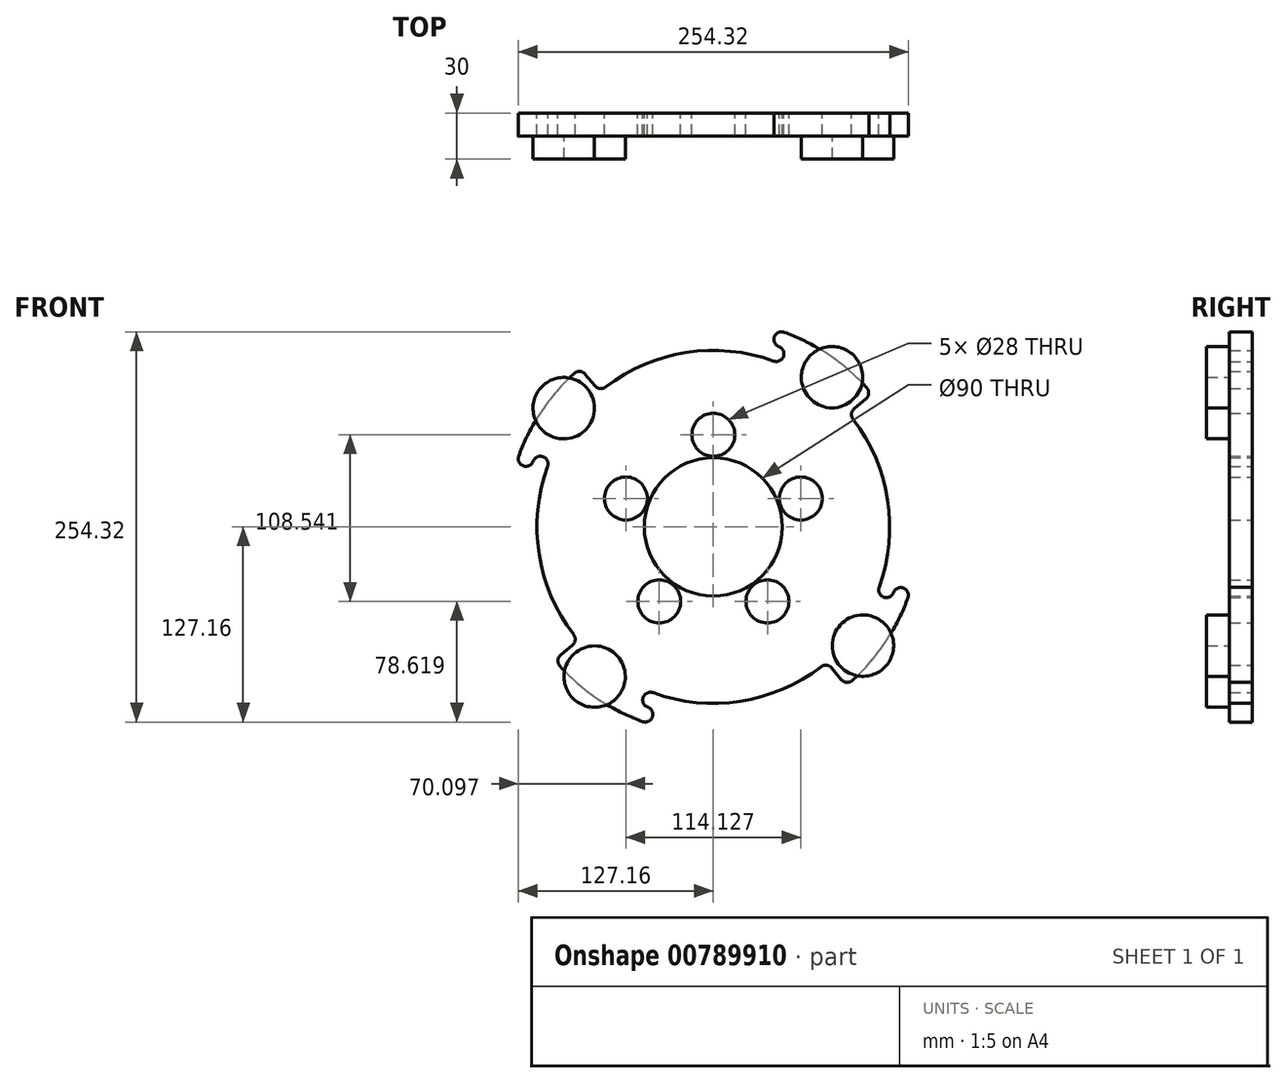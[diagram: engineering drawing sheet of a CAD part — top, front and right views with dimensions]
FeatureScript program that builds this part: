
annotation { "Feature Type Name" : "Feature", "Feature Type Description" : "" }
export const myFeature = defineFeature(function(context is Context, id is Id, definition is map)
    precondition{}
    {
        {
            var Q0;
            Q0=qCreatedBy(makeId("Front.planeOp"),FACE);
            var sketch = newSketch(context, id + "F0", { "sketchPlane" : qUnion([Q0])});
            skCircle(sketch, "E0", {"center": v(0, 0) * mm, "radius": 45 * mm});
            skCircle(sketch, "E1", {"center": v(0, 0) * mm, "radius": 60 * mm, "construction": true});
            skArc(sketch, "E2", {"start": v(-108.06, 39.33) * mm, "mid": v(-113.64, -17.6) * mm, "end": v(-91.1, -70.19) * mm});
            skArc(sketch, "E3", {"start": v(-90.69, 100) * mm, "mid": v(-112.05, 75.3) * mm, "end": v(-126.86, 46.17) * mm});
            skLineSegment(sketch, "E4", {"start": v(0, -160.96) * mm, "end": v(0, 165.3) * mm, "construction": true});
            skLineSegment(sketch, "E5", {"start": v(-181.36, 0) * mm, "end": v(230.59, 0) * mm, "construction": true});
            skLineSegment(sketch, "E6", {"start": v(0, 0) * mm, "end": v(-73.92, 88.1) * mm, "construction": true});
            skCircle(sketch, "E7", {"center": v(0, 60) * mm, "radius": 14 * mm});
            skCircle(sketch, "E8.1.0", {"center": v(-57.06, 18.54) * mm, "radius": 14 * mm});
            skCircle(sketch, "E8.2.0", {"center": v(-35.27, -48.54) * mm, "radius": 14 * mm});
            skCircle(sketch, "E8.3.0", {"center": v(35.27, -48.54) * mm, "radius": 14 * mm});
            skCircle(sketch, "E8.4.0", {"center": v(57.06, 18.54) * mm, "radius": 14 * mm});
            skLineSegment(sketch, "E9", {"start": v(0, 0) * mm, "end": v(-172.3, 62.71) * mm, "construction": true});
            skLineSegment(sketch, "E10", {"start": v(-77.07, 91.85) * mm, "end": v(-83.5, 99.51) * mm});
            skArc(sketch, "E11", {"start": v(-126.86, 46.17) * mm, "mid": v(-123.87, 39.76) * mm, "end": v(-117.46, 42.75) * mm});
            skArc(sketch, "E12", {"start": v(-108.06, 39.33) * mm, "mid": v(-111.05, 45.74) * mm, "end": v(-117.46, 42.75) * mm});
            skArc(sketch, "E13.1.0", {"start": v(-39.33, -108.06) * mm, "mid": v(-45.74, -111.05) * mm, "end": v(-42.75, -117.46) * mm});
            skArc(sketch, "E13.1.1", {"start": v(-46.17, -126.86) * mm, "mid": v(-39.76, -123.87) * mm, "end": v(-42.75, -117.46) * mm});
            skLineSegment(sketch, "E13.1.2", {"start": v(-91.85, -77.07) * mm, "end": v(-99.51, -83.5) * mm});
            skArc(sketch, "E13.2.0", {"start": v(108.06, -39.33) * mm, "mid": v(111.05, -45.74) * mm, "end": v(117.46, -42.75) * mm});
            skArc(sketch, "E13.2.1", {"start": v(126.86, -46.17) * mm, "mid": v(123.87, -39.76) * mm, "end": v(117.46, -42.75) * mm});
            skLineSegment(sketch, "E13.2.2", {"start": v(77.07, -91.85) * mm, "end": v(83.5, -99.51) * mm});
            skArc(sketch, "E13.3.0", {"start": v(39.33, 108.06) * mm, "mid": v(45.74, 111.05) * mm, "end": v(42.75, 117.46) * mm});
            skArc(sketch, "E13.3.1", {"start": v(46.17, 126.86) * mm, "mid": v(39.76, 123.87) * mm, "end": v(42.75, 117.46) * mm});
            skLineSegment(sketch, "E13.3.2", {"start": v(91.85, 77.07) * mm, "end": v(99.51, 83.5) * mm});
            skLineSegment(sketch, "E14.trimOffspring", {"start": v(-86.78, 103.42) * mm, "end": v(-114.3, 136.21) * mm, "construction": true});
            skArc(sketch, "E15.trimOffspring", {"start": v(100, 90.69) * mm, "mid": v(75.3, 112.05) * mm, "end": v(46.17, 126.86) * mm});
            skArc(sketch, "E16.trimOffspring", {"start": v(90.69, -100) * mm, "mid": v(112.05, -75.3) * mm, "end": v(126.86, -46.17) * mm});
            skArc(sketch, "E17.trimOffspring", {"start": v(-100, -90.69) * mm, "mid": v(-75.3, -112.05) * mm, "end": v(-46.17, -126.86) * mm});
            skPoint(sketch, "E18.visualSharp", {"position": v(-86.78, 103.42) * mm});
            skArc(sketch, "E18.filletArc", {"start": v(-83.5, 99.51) * mm, "mid": v(-87, 101.29) * mm, "end": v(-90.69, 100) * mm});
            skArc(sketch, "E19.trimOffspring", {"start": v(39.33, 108.06) * mm, "mid": v(-17.6, 113.64) * mm, "end": v(-70.19, 91.1) * mm});
            skArc(sketch, "E20.trimOffspring", {"start": v(108.06, -39.33) * mm, "mid": v(113.64, 17.6) * mm, "end": v(91.1, 70.19) * mm});
            skArc(sketch, "E21.trimOffspring", {"start": v(-39.33, -108.06) * mm, "mid": v(17.6, -113.64) * mm, "end": v(70.19, -91.1) * mm});
            skPoint(sketch, "E22.visualSharp", {"position": v(-73.92, 88.1) * mm});
            skArc(sketch, "E22.filletArc", {"start": v(-77.07, 91.85) * mm, "mid": v(-73.78, 90.09) * mm, "end": v(-70.19, 91.1) * mm});
            skPoint(sketch, "E23.visualSharp", {"position": v(-88.1, -73.92) * mm});
            skArc(sketch, "E23.filletArc", {"start": v(-91.85, -77.07) * mm, "mid": v(-90.09, -73.78) * mm, "end": v(-91.1, -70.19) * mm});
            skPoint(sketch, "E24.visualSharp", {"position": v(-103.42, -86.78) * mm});
            skArc(sketch, "E24.filletArc", {"start": v(-99.51, -83.5) * mm, "mid": v(-101.29, -87) * mm, "end": v(-100, -90.69) * mm});
            skPoint(sketch, "E25.visualSharp", {"position": v(73.92, -88.1) * mm});
            skArc(sketch, "E25.filletArc", {"start": v(77.07, -91.85) * mm, "mid": v(73.78, -90.09) * mm, "end": v(70.19, -91.1) * mm});
            skPoint(sketch, "E26.visualSharp", {"position": v(86.78, -103.42) * mm});
            skArc(sketch, "E26.filletArc", {"start": v(83.5, -99.51) * mm, "mid": v(87, -101.29) * mm, "end": v(90.69, -100) * mm});
            skPoint(sketch, "E27.visualSharp", {"position": v(103.42, 86.78) * mm});
            skArc(sketch, "E27.filletArc", {"start": v(99.51, 83.5) * mm, "mid": v(101.29, 87) * mm, "end": v(100, 90.69) * mm});
            skPoint(sketch, "E28.visualSharp", {"position": v(88.1, 73.92) * mm});
            skArc(sketch, "E28.filletArc", {"start": v(91.85, 77.07) * mm, "mid": v(90.09, 73.78) * mm, "end": v(91.1, 70.19) * mm});
            skSolve(sketch);
        }
        {
            var Q0;
            Q0=qSketchRegion(id+"F0",true);
            extrude(context, id + "F1", {"entities" : qUnion([Q0]), "depth" : 15 * mm, "offsetDistance" : 25 * mm});
        }
        {
            var Q0;
            Q0=makeQuery(id+"F1.opExtrude","CAP_FACE",FACE,{"disambiguationData":[OSD([sQuery(id+"F0.wireOp",EDGE,"E0"),sQuery(id+"F0.wireOp",EDGE,"E2"),sQuery(id+"F0.wireOp",EDGE,"E3"),sQuery(id+"F0.wireOp",EDGE,"E7"),sQuery(id+"F0.wireOp",EDGE,"E8.1.0"),sQuery(id+"F0.wireOp",EDGE,"E8.2.0"),sQuery(id+"F0.wireOp",EDGE,"E8.3.0"),sQuery(id+"F0.wireOp",EDGE,"E8.4.0"),sQuery(id+"F0.wireOp",EDGE,"E10"),sQuery(id+"F0.wireOp",EDGE,"E11"),sQuery(id+"F0.wireOp",EDGE,"E12"),sQuery(id+"F0.wireOp",EDGE,"E13.1.0"),sQuery(id+"F0.wireOp",EDGE,"E13.1.1"),sQuery(id+"F0.wireOp",EDGE,"E13.1.2"),sQuery(id+"F0.wireOp",EDGE,"E13.2.0"),sQuery(id+"F0.wireOp",EDGE,"E13.2.1"),sQuery(id+"F0.wireOp",EDGE,"E13.2.2"),sQuery(id+"F0.wireOp",EDGE,"E13.3.0"),sQuery(id+"F0.wireOp",EDGE,"E13.3.1"),sQuery(id+"F0.wireOp",EDGE,"E13.3.2"),sQuery(id+"F0.wireOp",EDGE,"E15.trimOffspring"),sQuery(id+"F0.wireOp",EDGE,"E16.trimOffspring"),sQuery(id+"F0.wireOp",EDGE,"E17.trimOffspring"),sQuery(id+"F0.wireOp",EDGE,"E18.filletArc"),sQuery(id+"F0.wireOp",EDGE,"E19.trimOffspring"),sQuery(id+"F0.wireOp",EDGE,"E20.trimOffspring"),sQuery(id+"F0.wireOp",EDGE,"E21.trimOffspring"),sQuery(id+"F0.wireOp",EDGE,"E22.filletArc"),sQuery(id+"F0.wireOp",EDGE,"E23.filletArc"),sQuery(id+"F0.wireOp",EDGE,"E24.filletArc"),sQuery(id+"F0.wireOp",EDGE,"E25.filletArc"),sQuery(id+"F0.wireOp",EDGE,"E26.filletArc"),sQuery(id+"F0.wireOp",EDGE,"E27.filletArc"),sQuery(id+"F0.wireOp",EDGE,"E28.filletArc")])],"isStart":false});
            var sketch = newSketch(context, id + "F2", { "sketchPlane" : qUnion([Q0])});
            skCircle(sketch, "E29", {"center": v(-97.55, 77.36) * mm, "radius": 20 * mm});
            skCircle(sketch, "E30", {"center": v(0, 0) * mm, "radius": 144.5 * mm, "construction": true});
            skLineSegment(sketch, "E31", {"start": v(-97.55, 77.36) * mm, "end": v(0, 0) * mm, "construction": true});
            skCircle(sketch, "E32.1.0", {"center": v(-77.36, -97.55) * mm, "radius": 20 * mm});
            skCircle(sketch, "E32.2.0", {"center": v(97.55, -77.36) * mm, "radius": 20 * mm});
            skCircle(sketch, "E32.3.0", {"center": v(77.36, 97.55) * mm, "radius": 20 * mm});
            skSolve(sketch);
        }
        {
            var Q0;
            {var subQ0=sQuery(id+"F2.wireOp",EDGE,"E29");var subQ1=makeQuery(id+"F1.opExtrude","CAP_EDGE",EDGE,{"disambiguationData":[OSD([sQuery(id+"F0.wireOp",EDGE,"E3")])],"isStart":false});var subQ2=makeQuery(id+"F2.imprint","INTERSECT",VERTEX,{"disambiguationData":[OD(0.0)],"derivedFrom":[subQ1,subQ0]});Q0=makeQuery(id+"F2.imprint","IMPRINT",FACE,{"disambiguationData":[TD([[makeQuery(id+"F2.imprint","IMPRINT",EDGE,{"disambiguationData":[TD([[subQ2,-1.0]])],"derivedFrom":subQ0}),1.0]])]});}
            var Q1;
            {var subQ0=sQuery(id+"F2.wireOp",EDGE,"E29");var subQ1=makeQuery(id+"F1.opExtrude","CAP_EDGE",EDGE,{"disambiguationData":[OSD([sQuery(id+"F0.wireOp",EDGE,"E3")])],"isStart":false});var subQ2=makeQuery(id+"F2.imprint","INTERSECT",VERTEX,{"disambiguationData":[OD(0.0)],"derivedFrom":[subQ1,subQ0]});Q1=makeQuery(id+"F2.imprint","IMPRINT",FACE,{"disambiguationData":[TD([[makeQuery(id+"F2.imprint","IMPRINT",EDGE,{"disambiguationData":[TD([[subQ2,1.0]])],"derivedFrom":subQ0}),1.0]])]});}
            extrude(context, id + "F3", {"entities" : qUnion([Q0, Q1]), "depth" : 15 * mm, "offsetDistance" : 25 * mm});
        }
        {
            var Q0;
            Q0=makeQuery(id+"F3.opExtrude","SWEPT_BODY",BODY,{"disambiguationData":[OSD([sQuery(id+"F2.wireOp",EDGE,"E29")])]});
            var Q1;
            Q1=makeQuery(id+"F1.opExtrude","CAP_EDGE",EDGE,{"disambiguationData":[OSD([sQuery(id+"F0.wireOp",EDGE,"E0")])],"isStart":false});
            circularPattern(context, id + "F4", {"operationType" : NewBodyOperationType.ADD, "entities" : qUnion([Q0]), "axis" : qUnion([Q1]), "angle" : 360 * degree, "instanceCount" : 4, "equalSpace" : true, "computeTransformsWithoutBuiltin" : true});
        }
    });
